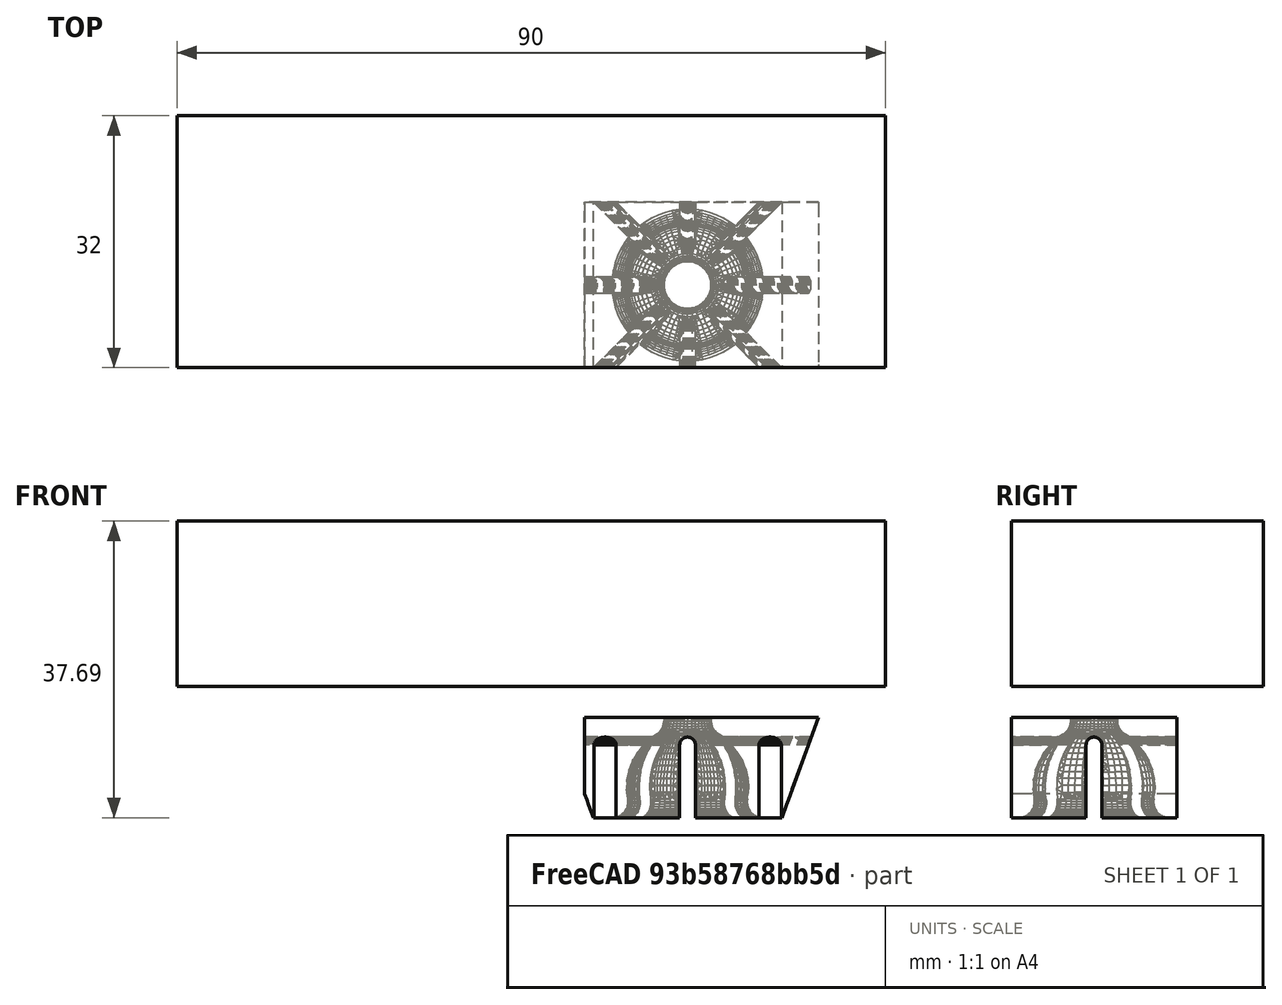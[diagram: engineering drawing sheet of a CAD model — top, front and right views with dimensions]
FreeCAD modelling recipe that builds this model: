
FCSTD DOCUMENT  (FreeCAD 0.18R14555 (Git shallow))
Label: camera-mounter
License: All rights reserved
LicenseURL: http://en.wikipedia.org/wiki/All_rights_reserved
objects: Part::Box×7, Part::Cylinder×5, Part::Feature×4, Part::Cut×4, Part::MultiFuse×3, Part::Chamfer×3, Mesh::Feature×1, Part::MultiCommon×1, Part::Fillet×1
note: 28 computed .brp shape members not serialized (recipe doc carries the construction recipe); baked Part::Feature solids carry a one-line shape summary decoded from their .brp

FEATURE [Mesh::Feature] raspiCamBack
FEATURE [Part::Feature] raspiCamBack001
  shape: bbox 33.4 x 32.4 x 24 mm, 16508 faces, 0 solids (baked)
FEATURE [Part::Feature] raspiCamBack001001  label="raspiCamBack002"
  shape: bbox 33.4 x 32.4 x 24 mm, 14812 faces, 0 solids (baked)
FEATURE [Part::Feature] raspiCamBack001001_solid  label="raspiCamBack002 (Solid)"
  shape: bbox 33.4 x 32.4 x 24 mm, 14812 faces (baked)
FEATURE [Part::Box] Box  label="Cube"
  AttacherType = Attacher::AttachEngine3D
  Height = 27
  Length = 43
  Placement = pos=(-5,-6,13) rot=(0,0,1;0rad)
  Width = 52
FEATURE [Part::Cut] Cut  label="mounter"
  Base = -> raspiCamBack001001_solid
  Placement = pos=(-3.806,-5.872,-0.051) rot=(0,0,1;0rad)
  Tool = -> Box
FEATURE [Part::Box] Box001  label="Cube001"
  AttacherType = Attacher::AttachEngine3D
  Height = 13
  Length = 72.5
  Width = 21
FEATURE [Part::Box] Box002  label="Cube002"
  AttacherType = Attacher::AttachEngine3D
  Height = 5
  Length = 72.5
  Placement = pos=(-43,0,13) rot=(0,0,1;0rad)
  Width = 21
FEATURE [Part::MultiCommon] Common
  Placement = pos=(-0.2,0,0.1) rot=(0,0,1;0rad)
  Shapes = -> [Cut,Box001]
FEATURE [Part::Box] Box003  label="Cube003"
  AttacherType = Attacher::AttachEngine3D
  Height = 16
  Length = 6
  Placement = pos=(-43,0,18) rot=(0,0,1;0rad)
  Width = 21
FEATURE [Part::Cylinder] Cylinder
  Angle = 360
  AttacherType = Attacher::AttachEngine3D
  Height = 10
  Placement = pos=(-22,10.3751,12) rot=(0,0,1;0rad)
  Radius = 8
FEATURE [Part::Cylinder] Cylinder001
  Angle = 360
  AttacherType = Attacher::AttachEngine3D
  Height = 30
  Placement = pos=(-54,10.5,27) rot=(0,1,0;1.5708rad)
  Radius = 2
FEATURE [Part::Box] Box004  label="Cube004"
  AttacherType = Attacher::AttachEngine3D
  Height = 21
  Length = 90
  Placement = pos=(-52,0,17) rot=(0,0,1;0rad)
  Width = 32
FEATURE [Part::Cylinder] Cylinder002
  Angle = 360
  AttacherType = Attacher::AttachEngine3D
  Height = 10
  Placement = pos=(-10,10.3751,12) rot=(0,0,1;0rad)
  Radius = 8
FEATURE [Part::Box] Box005  label="Cube005"
  AttacherType = Attacher::AttachEngine3D
  Height = 10
  Length = 12
  Placement = pos=(-22,2.4,12) rot=(0,0,1;0rad)
  Width = 16
FEATURE [Part::MultiFuse] Fusion
  Shapes = -> [Box005,Cylinder002,Cylinder]
FEATURE [Part::Fillet] Fillet
  Base = -> Box003
  Edges = 2 edges r=4: [Edge10,Edge12]
FEATURE [Part::Box] Box006  label="Cube006"
  AttacherType = Attacher::AttachEngine3D
  Height = 4
  Length = 5
  Width = 6
FEATURE [Part::Cylinder] Cylinder003
  Angle = 360
  AttacherType = Attacher::AttachEngine3D
  Height = 5
  Placement = pos=(9e-16,3,-7e-16) rot=(0.57735,0.57735,0.57735;2.0944rad)
  Radius = 3
FEATURE [Part::Cylinder] Cylinder004
  Angle = 360
  AttacherType = Attacher::AttachEngine3D
  Height = 5
  Placement = pos=(1e-15,3,-1e-15) rot=(0.57735,0.57735,0.57735;2.0944rad)
  Radius = 1.575
  expr: Radius = 3.15 / 2
FEATURE [Part::MultiFuse] Fusion001
  Shapes = -> [Cylinder003,Box006]
FEATURE [Part::Cut] Cut004
  Base = -> Fusion001
  Placement = pos=(1,15,10) rot=(0,0,1;0rad)
  Tool = -> Cylinder004
FEATURE [Part::Chamfer] Chamfer
  Base = -> Box002
  Edges = 7 edges r=1: [Edge4,Edge5,Edge6,Edge7,Edge8,Edge9,Edge11]
FEATURE [Part::Cut] Cut005
  Base = -> Chamfer
  Tool = -> Fusion
FEATURE [Part::Cut] Cut006
  Base = -> Fillet
  Tool = -> Cylinder001
FEATURE [Part::MultiFuse] Fusion002
  Shapes = -> [Cut005,Cut004,Cut006]
FEATURE [Part::Chamfer] Chamfer001
  Base = -> Fusion002
  Edges = 7 edges r=1: [Edge1,Edge4,Edge12,Edge13,Edge14,Edge15,Edge16]
FEATURE [Part::Chamfer] Chamfer002
  Base = -> Chamfer001
  Edges = 5 edges r=0.5: [Edge33,Edge35,Edge36,Edge37,Edge39]
FEATURE [Part::Feature] Chamfer002_solid  label="Chamfer002 (Solid)"
  shape: bbox 72.62 x 21.12 x 27.12 mm, 57 faces (baked)
